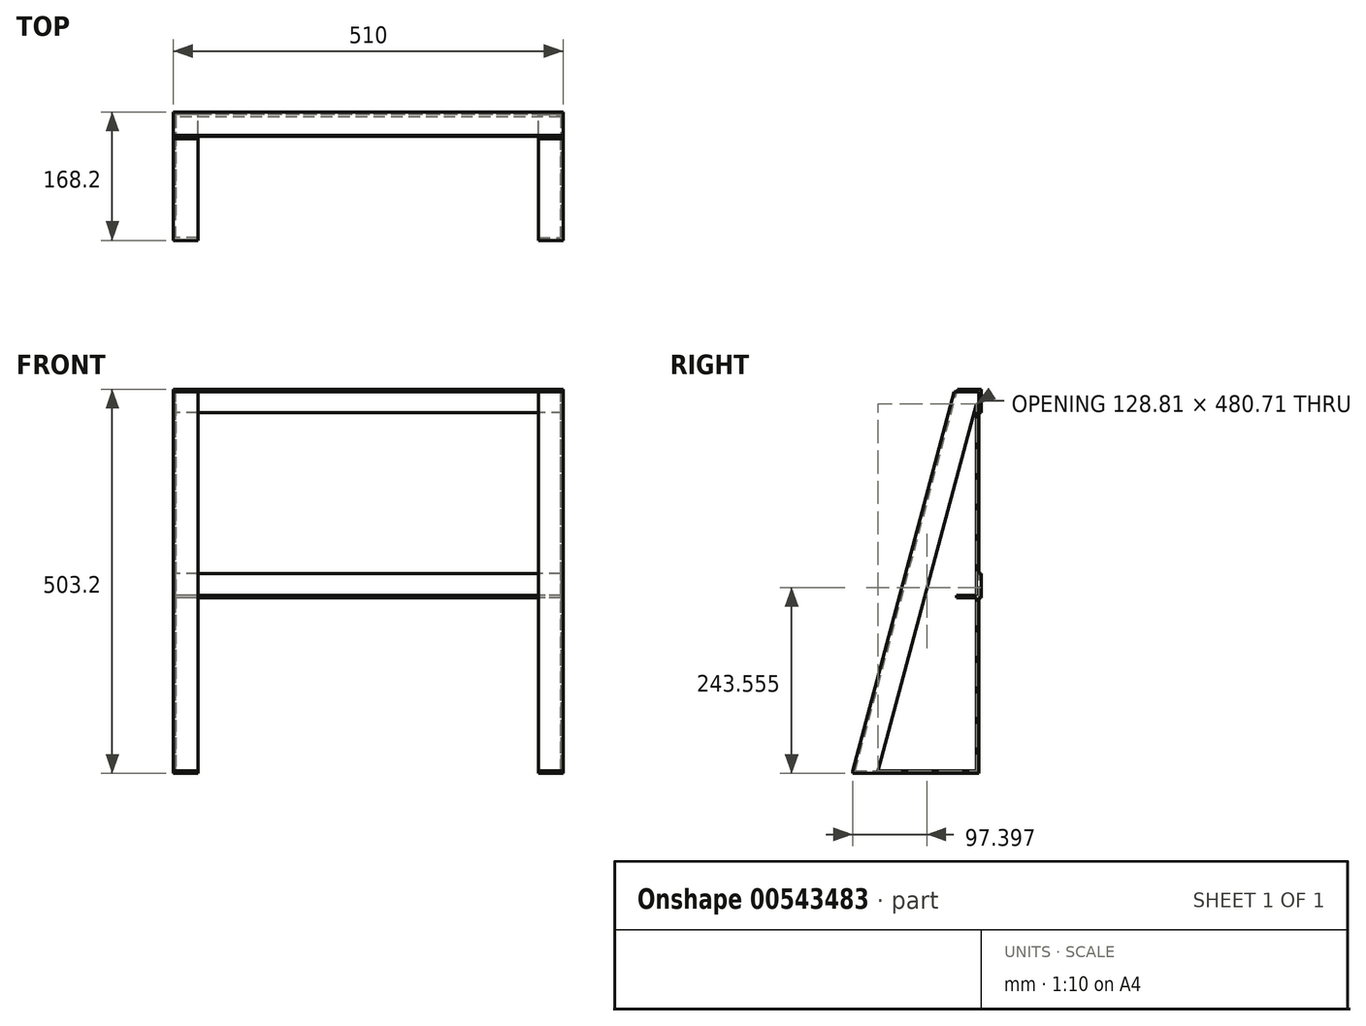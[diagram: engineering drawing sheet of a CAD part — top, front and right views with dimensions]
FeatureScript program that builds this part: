
annotation { "Feature Type Name" : "Feature", "Feature Type Description" : "" }
export const myFeature = defineFeature(function(context is Context, id is Id, definition is map)
    precondition{}
    {
        {
            var Q0;
            Q0=qCreatedBy(makeId("Right.planeOp"),FACE);
            var sketch = newSketch(context, id + "F0", { "sketchPlane" : qUnion([Q0])});
            skLineSegment(sketch, "E0", {"start": v(-165, 0) * mm, "end": v(0, 0) * mm});
            skLineSegment(sketch, "E1", {"start": v(0, 0) * mm, "end": v(0, 500) * mm});
            skLineSegment(sketch, "E2", {"start": v(0, 500) * mm, "end": v(-31.87, 500) * mm});
            skLineSegment(sketch, "E3", {"start": v(-31.87, 500) * mm, "end": v(-31.87, 31.87) * mm});
            skLineSegment(sketch, "E4", {"start": v(-31.87, 31.87) * mm, "end": v(-165, 31.87) * mm});
            skLineSegment(sketch, "E5", {"start": v(-165, 31.87) * mm, "end": v(-165, 0) * mm});
            skLineSegment(sketch, "E6.top", {"start": v(-165, 3.2) * mm, "end": v(0, 3.2) * mm});
            skLineSegment(sketch, "E6.left", {"start": v(-165, 0) * mm, "end": v(-165, 3.2) * mm});
            skLineSegment(sketch, "E6.right", {"start": v(0, 0) * mm, "end": v(0, 3.2) * mm});
            skLineSegment(sketch, "E7.bottom", {"start": v(0, 0) * mm, "end": v(-3.2, 0) * mm});
            skLineSegment(sketch, "E7.top", {"start": v(0, 500) * mm, "end": v(-3.2, 500) * mm});
            skLineSegment(sketch, "E7.right", {"start": v(-3.2, 0) * mm, "end": v(-3.2, 500) * mm});
            skSolve(sketch);
        }
        {
            var Q0;
            {var subQ2=sQuery(id+"F0.wireOp",EDGE,"E2");Q0=makeQuery(id+"F0.imprint","IMPRINT",FACE,{"disambiguationData":[TD([[makeQuery(id+"F0.imprint","IMPRINT",EDGE,{"derivedFrom":subQ2}),1.0]])]});}
            extrude(context, id + "F1", {"entities" : qUnion([Q0]), "depth" : 3.2 * mm, "offsetDistance" : 25 * mm});
        }
        {
            var Q0;
            {var subQ0=sQuery(id+"F0.wireOp",EDGE,"E0");Q0=makeQuery(id+"F0.imprint","IMPRINT",FACE,{"disambiguationData":[TD([[makeQuery(id+"F0.imprint","IMPRINT",EDGE,{"derivedFrom":subQ0}),1.0]])]});}
            var Q1;
            {var subQ5=sQuery(id+"F0.wireOp",EDGE,"E7.bottom");Q1=makeQuery(id+"F0.imprint","IMPRINT",FACE,{"disambiguationData":[TD([[makeQuery(id+"F0.imprint","IMPRINT",EDGE,{"derivedFrom":subQ5}),-1.0]])]});}
            var Q2;
            {var subQ5=sQuery(id+"F0.wireOp",EDGE,"E7.top");Q2=makeQuery(id+"F0.imprint","IMPRINT",FACE,{"disambiguationData":[TD([[makeQuery(id+"F0.imprint","IMPRINT",EDGE,{"derivedFrom":subQ5}),1.0]])]});}
            extrude(context, id + "F2", {"entities" : qUnion([Q0, Q1, Q2]), "operationType" : NewBodyOperationType.ADD, "depth" : 31.87 * mm, "offsetDistance" : 25 * mm});
        }
        {
            var Q0;
            {var subQ2=sQuery(id+"F0.wireOp",EDGE,"E2");Q0=makeQuery(id+"F0.imprint","IMPRINT",FACE,{"disambiguationData":[TD([[makeQuery(id+"F0.imprint","IMPRINT",EDGE,{"derivedFrom":subQ2}),1.0]])]});}
            var sketch = newSketch(context, id + "F3", { "sketchPlane" : qUnion([Q0])});
            skLineSegment(sketch, "E8.0", {"start": v(-3.2, 3.2) * mm, "end": v(-3.2, 500) * mm});
            skLineSegment(sketch, "E9.0", {"start": v(-165, 3.2) * mm, "end": v(-3.2, 3.2) * mm});
            skPoint(sketch, "E10.orphan", {"position": v(0, 3.2) * mm});
            skPoint(sketch, "E11.orphan", {"position": v(-3.2, 0) * mm});
            skLineSegment(sketch, "E12", {"start": v(-3.2, 607.05) * mm, "end": v(-165, 3.2) * mm});
            skLineSegment(sketch, "E13", {"start": v(-3.2, 483.9) * mm, "end": v(-132, 3.2) * mm});
            skLineSegment(sketch, "E14", {"start": v(-161.69, 3.2) * mm, "end": v(-3.2, 594.68) * mm});
            skLineSegment(sketch, "E15.0", {"start": v(0, 500) * mm, "end": v(-31.87, 500) * mm});
            skLineSegment(sketch, "E16", {"start": v(-28.57, 500) * mm, "end": v(-33.17, 500) * mm});
            skSolve(sketch);
        }
        {
            var Q0;
            {var subQ0=sQuery(id+"F3.wireOp",EDGE,"E13");Q0=makeQuery(id+"F3.imprint","IMPRINT",FACE,{"disambiguationData":[TD([[makeQuery(id+"F3.imprint","IMPRINT",EDGE,{"derivedFrom":subQ0}),-1.0]])]});}
            extrude(context, id + "F4", {"entities" : qUnion([Q0]), "depth" : 3.2 * mm, "offsetDistance" : 25 * mm});
        }
        {
            var Q0;
            {var subQ1=sQuery(id+"F3.wireOp",EDGE,"E9.0");var subQ3=sQuery(id+"F3.wireOp",EDGE,"E14");var subQ4=makeQuery(id+"F3.imprint","INTERSECT",VERTEX,{"derivedFrom":[subQ1,subQ3]});Q0=makeQuery(id+"F3.imprint","IMPRINT",FACE,{"disambiguationData":[TD([[makeQuery(id+"F3.imprint","IMPRINT",EDGE,{"disambiguationData":[TD([[subQ4,-1.0]])],"derivedFrom":subQ3}),1.0]])]});}
            var Q1;
            {var subQ0=sQuery(id+"F3.wireOp",EDGE,"E16");var subQ5=sQuery(id+"F3.wireOp",EDGE,"E12");var subQ6=makeQuery(id+"F3.imprint","INTERSECT",VERTEX,{"derivedFrom":[subQ5,subQ0]});Q1=makeQuery(id+"F3.imprint","IMPRINT",FACE,{"disambiguationData":[TD([[makeQuery(id+"F3.imprint","IMPRINT",EDGE,{"disambiguationData":[TD([[subQ6,-1.0]])],"derivedFrom":subQ5}),1.0]])]});}
            var Q2;
            {var subQ0=sQuery(id+"F3.wireOp",EDGE,"E16");var subQ3=makeQuery(id+"F0.imprint","IMPRINT",EDGE,{"derivedFrom":sQuery(id+"F0.wireOp",EDGE,"E3")});var subQ5=makeQuery(id+"F3.imprint","INTERSECT",VERTEX,{"derivedFrom":[subQ3,subQ0]});Q2=makeQuery(id+"F3.imprint","IMPRINT",FACE,{"disambiguationData":[TD([[makeQuery(id+"F3.imprint","IMPRINT",EDGE,{"disambiguationData":[TD([[subQ5,-1.0]])],"derivedFrom":subQ3}),1.0]])]});}
            extrude(context, id + "F5", {"entities" : qUnion([Q0, Q1, Q2]), "depth" : 31.87 * mm, "offsetDistance" : 25 * mm});
        }
        {
            var Q0;
            Q0=makeQuery(id+"F1.opExtrude","SWEPT_BODY",BODY,{"disambiguationData":[OSD([sQuery(id+"F0.wireOp",EDGE,"E2"),sQuery(id+"F0.wireOp",EDGE,"E3"),sQuery(id+"F0.wireOp",EDGE,"E4"),sQuery(id+"F0.wireOp",EDGE,"E5"),sQuery(id+"F0.wireOp",EDGE,"E6.top"),sQuery(id+"F0.wireOp",EDGE,"E7.right")])]});
            var Q1;
            Q1=makeQuery(id+"F4.opExtrude","SWEPT_BODY",BODY,{"disambiguationData":[OSD([sQuery(id+"F3.wireOp",EDGE,"E8.0"),sQuery(id+"F3.wireOp",EDGE,"E9.0"),sQuery(id+"F3.wireOp",EDGE,"E13"),sQuery(id+"F3.wireOp",EDGE,"E14")])]});
            var Q2;
            Q2=makeQuery(id+"F5.opExtrude","SWEPT_BODY",BODY,{"disambiguationData":[OSD([sQuery(id+"F3.wireOp",EDGE,"E8.0"),sQuery(id+"F3.wireOp",EDGE,"E9.0"),sQuery(id+"F3.wireOp",EDGE,"E12"),sQuery(id+"F3.wireOp",EDGE,"E14")])]});
            booleanBodies(context, id + "F6", {"operationType" : BooleanOperationType.UNION, "tools" : qUnion([Q0, Q1, Q2])});
        }
        {
            var Q0;
            {var subQ2=sQuery(id+"F0.wireOp",EDGE,"E2");Q0=makeQuery(id+"F0.imprint","IMPRINT",FACE,{"disambiguationData":[TD([[makeQuery(id+"F0.imprint","IMPRINT",EDGE,{"derivedFrom":subQ2}),1.0]])]});}
            cPlane(context, id + "F7", {"entities" : qUnion([Q0]), "cplaneType" : CPlaneType.OFFSET, "offset" : 255 * mm, "width" : 150 * mm, "height" : 150 * mm});
        }
        {
            var Q0;
            Q0=makeQuery(id+"F1.opExtrude","SWEPT_BODY",BODY,{"disambiguationData":[OSD([sQuery(id+"F0.wireOp",EDGE,"E2"),sQuery(id+"F0.wireOp",EDGE,"E3"),sQuery(id+"F0.wireOp",EDGE,"E4"),sQuery(id+"F0.wireOp",EDGE,"E5"),sQuery(id+"F0.wireOp",EDGE,"E6.top"),sQuery(id+"F0.wireOp",EDGE,"E7.right")])]});
            var Q1;
            Q1=qCreatedBy(id+"F7.planeOp",FACE);
            mirror(context, id + "F8", {"entities" : qUnion([Q0]), "mirrorPlane" : qUnion([Q1])});
        }
        {
            var Q0;
            {var subQ0=sQuery(id+"F0.wireOp",EDGE,"E7.right");var subQ1=sQuery(id+"F0.wireOp",EDGE,"E2");var subQ2=sQuery(id+"F0.wireOp",EDGE,"E3");Q0=makeQuery(id+"F6.opBoolean","SPLIT",FACE,{"disambiguationData":[TD([makeQuery(id+"F1.opExtrude","SWEPT_FACE",FACE,{"disambiguationData":[OSD([subQ1])]})])],"derivedFrom":makeQuery(id+"F1.opExtrude","CAP_FACE",FACE,{"disambiguationData":[OSD([subQ1,subQ2,sQuery(id+"F0.wireOp",EDGE,"E4"),sQuery(id+"F0.wireOp",EDGE,"E5"),sQuery(id+"F0.wireOp",EDGE,"E6.top"),subQ0])],"isStart":false})});}
            var sketch = newSketch(context, id + "F9", { "sketchPlane" : qUnion([Q0])});
            skPoint(sketch, "E17.0.start.orphan", {"position": v(-3.2, 3.2) * mm});
            skPoint(sketch, "E18.orphan", {"position": v(0, 0) * mm});
            skLineSegment(sketch, "E19.0", {"start": v(-31.87, 500.05) * mm, "end": v(-165, 3.2) * mm});
            skLineSegment(sketch, "E20.0", {"start": v(-161.69, 3.2) * mm, "end": v(-28.57, 500) * mm});
            skLineSegment(sketch, "E21.0", {"start": v(-165, 3.2) * mm, "end": v(-3.2, 3.2) * mm});
            skLineSegment(sketch, "E22.0", {"start": v(-31.87, 31.87) * mm, "end": v(-165, 31.87) * mm});
            skPoint(sketch, "E23.orphan", {"position": v(-3.2, 607.05) * mm});
            skPoint(sketch, "E24.orphan", {"position": v(-3.2, 594.68) * mm});
            skLineSegment(sketch, "E25.0", {"start": v(-28.57, 500) * mm, "end": v(-31.88, 500) * mm});
            skPoint(sketch, "E26.orphan", {"position": v(0, 500) * mm});
            skLineSegment(sketch, "E27", {"start": v(0, 500) * mm, "end": v(-27.67, 500) * mm});
            skLineSegment(sketch, "E28", {"start": v(-27.67, 500) * mm, "end": v(-27.67, 503.2) * mm});
            skLineSegment(sketch, "E29", {"start": v(-27.67, 503.2) * mm, "end": v(3.2, 503.2) * mm});
            skLineSegment(sketch, "E30", {"start": v(3.2, 503.2) * mm, "end": v(3.2, 472.33) * mm});
            skLineSegment(sketch, "E31", {"start": v(3.2, 472.33) * mm, "end": v(0, 472.33) * mm});
            skLineSegment(sketch, "E32", {"start": v(0, 472.33) * mm, "end": v(0, 500) * mm});
            skSolve(sketch);
        }
        {
            var Q0;
            Q0=makeQuery(id+"F9.imprint","IMPRINT",FACE,{"disambiguationData":[TD([[makeQuery(id+"F9.imprint","IMPRINT",EDGE,{"derivedFrom":sQuery(id+"F9.wireOp",EDGE,"E27")}),-1.0]])]});
            var Q1;
            {var subQ0=sQuery(id+"F3.wireOp",EDGE,"E14");var subQ1=sQuery(id+"F3.wireOp",EDGE,"E9.0");var subQ2=sQuery(id+"F3.wireOp",EDGE,"E8.0");var subQ3=sQuery(id+"F0.wireOp",EDGE,"E7.right");var subQ4=sQuery(id+"F0.wireOp",EDGE,"E6.top");Q1=makeQuery(id+"F8.opPattern","COPY",FACE,{"derivedFrom":makeQuery(id+"F6.opBoolean","MERGE",FACE,{"derivedFrom":[makeQuery(id+"F2.boolean.opBoolean","MERGE",FACE,{"derivedFrom":[makeQuery(id+"F1.opExtrude","CAP_FACE",FACE,{"disambiguationData":[OSD([sQuery(id+"F0.wireOp",EDGE,"E2"),sQuery(id+"F0.wireOp",EDGE,"E3"),sQuery(id+"F0.wireOp",EDGE,"E4"),sQuery(id+"F0.wireOp",EDGE,"E5"),subQ4,subQ3])],"isStart":true}),makeQuery(id+"F2.opExtrude","CAP_FACE",FACE,{"disambiguationData":[OSD([sQuery(id+"F0.wireOp",EDGE,"E0"),subQ4,sQuery(id+"F0.wireOp",EDGE,"E6.left"),sQuery(id+"F0.wireOp",EDGE,"E7.bottom"),sQuery(id+"F0.wireOp",EDGE,"E7.top"),sQuery(id+"F0.wireOp",EDGE,"E1"),subQ3])],"isStart":true})]}),makeQuery(id+"F4.opExtrude","CAP_FACE",FACE,{"disambiguationData":[OSD([subQ2,subQ1,sQuery(id+"F3.wireOp",EDGE,"E13"),subQ0])],"isStart":true}),makeQuery(id+"F5.opExtrude","CAP_FACE",FACE,{"disambiguationData":[OSD([subQ2,subQ1,sQuery(id+"F3.wireOp",EDGE,"E12"),subQ0])],"isStart":true})]}),"instanceName":"1"});}
            var Q2;
            {var subQ0=sQuery(id+"F3.wireOp",EDGE,"E14");var subQ1=sQuery(id+"F3.wireOp",EDGE,"E9.0");var subQ2=sQuery(id+"F3.wireOp",EDGE,"E8.0");var subQ3=sQuery(id+"F0.wireOp",EDGE,"E7.right");var subQ4=sQuery(id+"F0.wireOp",EDGE,"E6.top");Q2=makeQuery(id+"F6.opBoolean","MERGE",FACE,{"derivedFrom":[makeQuery(id+"F2.boolean.opBoolean","MERGE",FACE,{"derivedFrom":[makeQuery(id+"F1.opExtrude","CAP_FACE",FACE,{"disambiguationData":[OSD([sQuery(id+"F0.wireOp",EDGE,"E2"),sQuery(id+"F0.wireOp",EDGE,"E3"),sQuery(id+"F0.wireOp",EDGE,"E4"),sQuery(id+"F0.wireOp",EDGE,"E5"),subQ4,subQ3])],"isStart":true}),makeQuery(id+"F2.opExtrude","CAP_FACE",FACE,{"disambiguationData":[OSD([sQuery(id+"F0.wireOp",EDGE,"E0"),subQ4,sQuery(id+"F0.wireOp",EDGE,"E6.left"),sQuery(id+"F0.wireOp",EDGE,"E7.bottom"),sQuery(id+"F0.wireOp",EDGE,"E7.top"),sQuery(id+"F0.wireOp",EDGE,"E1"),subQ3])],"isStart":true})]}),makeQuery(id+"F4.opExtrude","CAP_FACE",FACE,{"disambiguationData":[OSD([subQ2,subQ1,sQuery(id+"F3.wireOp",EDGE,"E13"),subQ0])],"isStart":true}),makeQuery(id+"F5.opExtrude","CAP_FACE",FACE,{"disambiguationData":[OSD([subQ2,subQ1,sQuery(id+"F3.wireOp",EDGE,"E12"),subQ0])],"isStart":true})]});}
            extrude(context, id + "F10", {"entities" : qUnion([Q0]), "endBound" : BoundingType.UP_TO_SURFACE, "depth" : 25 * mm, "endBoundEntityFace" : qUnion([Q1]), "offsetDistance" : 25 * mm, "hasSecondDirection" : true, "secondDirectionBound" : BoundingType.UP_TO_SURFACE, "secondDirectionOppositeDirection" : true, "secondDirectionDepth" : 25 * mm, "secondDirectionBoundEntityFace" : qUnion([Q2])});
        }
        {
            var Q0;
            {var subQ0=sQuery(id+"F3.wireOp",EDGE,"E14");var subQ1=sQuery(id+"F3.wireOp",EDGE,"E9.0");var subQ2=sQuery(id+"F0.wireOp",EDGE,"E3");var subQ3=sQuery(id+"F0.wireOp",EDGE,"E7.right");var subQ4=sQuery(id+"F0.wireOp",EDGE,"E6.top");Q0=qUnion([makeQuery(id+"F6.opBoolean","MERGE",FACE,{"derivedFrom":[makeQuery(id+"F2.boolean.opBoolean","MERGE",FACE,{"derivedFrom":[makeQuery(id+"F1.opExtrude","CAP_FACE",FACE,{"disambiguationData":[OSD([sQuery(id+"F0.wireOp",EDGE,"E2"),subQ2,sQuery(id+"F0.wireOp",EDGE,"E4"),sQuery(id+"F0.wireOp",EDGE,"E5"),subQ4,subQ3])],"isStart":true}),makeQuery(id+"F2.opExtrude","CAP_FACE",FACE,{"disambiguationData":[OSD([sQuery(id+"F0.wireOp",EDGE,"E0"),subQ4,sQuery(id+"F0.wireOp",EDGE,"E6.left"),sQuery(id+"F0.wireOp",EDGE,"E7.bottom"),sQuery(id+"F0.wireOp",EDGE,"E7.top"),sQuery(id+"F0.wireOp",EDGE,"E1"),subQ3])],"isStart":true})]}),makeQuery(id+"F4.opExtrude","CAP_FACE",FACE,{"disambiguationData":[OSD([subQ2,subQ1,sQuery(id+"F3.wireOp",EDGE,"E13"),subQ0])],"isStart":true}),makeQuery(id+"F5.opExtrude","CAP_FACE",FACE,{"disambiguationData":[OSD([subQ1,sQuery(id+"F3.wireOp",EDGE,"E12"),subQ0,sQuery(id+"F3.wireOp",EDGE,"E16")])],"isStart":true})]}),makeQuery(id+"F10.opExtrude","CAP_FACE",FACE,{"disambiguationData":[OSD([sQuery(id+"F9.wireOp",EDGE,"E27"),sQuery(id+"F9.wireOp",EDGE,"E28"),sQuery(id+"F9.wireOp",EDGE,"E29"),sQuery(id+"F9.wireOp",EDGE,"E30"),sQuery(id+"F9.wireOp",EDGE,"E31"),sQuery(id+"F9.wireOp",EDGE,"E32")])],"isStart":true})]);}
            var sketch = newSketch(context, id + "F11", { "sketchPlane" : qUnion([Q0])});
            skLineSegment(sketch, "E33", {"start": v(-3.2, 230) * mm, "end": v(28.67, 230) * mm});
            skLineSegment(sketch, "E34", {"start": v(28.67, 230) * mm, "end": v(28.67, 233.2) * mm});
            skLineSegment(sketch, "E35", {"start": v(-3.2, 261.87) * mm, "end": v(-3.2, 230) * mm});
            skLineSegment(sketch, "E36", {"start": v(-3.2, 261.87) * mm, "end": v(0, 261.87) * mm});
            skLineSegment(sketch, "E37", {"start": v(28.67, 233.2) * mm, "end": v(0, 233.2) * mm});
            skLineSegment(sketch, "E38", {"start": v(0, 233.2) * mm, "end": v(0, 261.87) * mm});
            skSolve(sketch);
        }
        {
            var Q0;
            {var subQ1=sQuery(id+"F11.wireOp",EDGE,"E35");Q0=makeQuery(id+"F11.imprint","IMPRINT",FACE,{"disambiguationData":[TD([[makeQuery(id+"F11.imprint","IMPRINT",EDGE,{"derivedFrom":subQ1}),1.0]])]});}
            var Q1;
            {var subQ0=sQuery(id+"F11.wireOp",EDGE,"E34");Q1=makeQuery(id+"F11.imprint","IMPRINT",FACE,{"disambiguationData":[TD([[makeQuery(id+"F11.imprint","IMPRINT",EDGE,{"derivedFrom":subQ0}),1.0]])]});}
            var Q2;
            {var subQ0=sQuery(id+"F3.wireOp",EDGE,"E14");var subQ1=sQuery(id+"F3.wireOp",EDGE,"E9.0");var subQ2=sQuery(id+"F0.wireOp",EDGE,"E3");var subQ3=sQuery(id+"F0.wireOp",EDGE,"E7.right");var subQ4=sQuery(id+"F0.wireOp",EDGE,"E6.top");Q2=qUnion([makeQuery(id+"F8.opPattern","COPY",FACE,{"derivedFrom":makeQuery(id+"F6.opBoolean","MERGE",FACE,{"derivedFrom":[makeQuery(id+"F2.boolean.opBoolean","MERGE",FACE,{"derivedFrom":[makeQuery(id+"F1.opExtrude","CAP_FACE",FACE,{"disambiguationData":[OSD([sQuery(id+"F0.wireOp",EDGE,"E2"),subQ2,sQuery(id+"F0.wireOp",EDGE,"E4"),sQuery(id+"F0.wireOp",EDGE,"E5"),subQ4,subQ3])],"isStart":true}),makeQuery(id+"F2.opExtrude","CAP_FACE",FACE,{"disambiguationData":[OSD([sQuery(id+"F0.wireOp",EDGE,"E0"),subQ4,sQuery(id+"F0.wireOp",EDGE,"E6.left"),sQuery(id+"F0.wireOp",EDGE,"E7.bottom"),sQuery(id+"F0.wireOp",EDGE,"E7.top"),sQuery(id+"F0.wireOp",EDGE,"E1"),subQ3])],"isStart":true})]}),makeQuery(id+"F4.opExtrude","CAP_FACE",FACE,{"disambiguationData":[OSD([subQ2,subQ1,sQuery(id+"F3.wireOp",EDGE,"E13"),subQ0])],"isStart":true}),makeQuery(id+"F5.opExtrude","CAP_FACE",FACE,{"disambiguationData":[OSD([subQ1,sQuery(id+"F3.wireOp",EDGE,"E12"),subQ0,sQuery(id+"F3.wireOp",EDGE,"E16")])],"isStart":true})]}),"instanceName":"1"}),makeQuery(id+"F10.opExtrude","CAP_FACE",FACE,{"disambiguationData":[OSD([sQuery(id+"F9.wireOp",EDGE,"E27"),sQuery(id+"F9.wireOp",EDGE,"E28"),sQuery(id+"F9.wireOp",EDGE,"E29"),sQuery(id+"F9.wireOp",EDGE,"E30"),sQuery(id+"F9.wireOp",EDGE,"E31"),sQuery(id+"F9.wireOp",EDGE,"E32")])],"isStart":false})]);}
            extrude(context, id + "F12", {"entities" : qUnion([Q0, Q1]), "operationType" : NewBodyOperationType.ADD, "endBound" : BoundingType.UP_TO_SURFACE, "oppositeDirection" : true, "depth" : 25 * mm, "endBoundEntityFace" : qUnion([Q2]), "offsetDistance" : 25 * mm});
        }
    });
